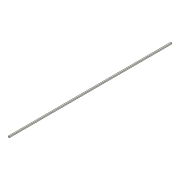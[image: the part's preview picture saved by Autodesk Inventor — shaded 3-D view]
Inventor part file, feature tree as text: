
AUTODESK INVENTOR PART (.ipt)
format: ipt  version: 2018 (Build 220112000, 112)  size: 71,680 bytes
history: native  units: in
note: dims shown in document units (in); Inventor stores cm internally (conversion verified against a paired STEP export)
features: extrude x1, sketch x1
ambient origin geometry x8: Origin, YZ Plane, XZ Plane, XY Plane, X Axis, Y Axis, Z Axis, Center Point
bodies: Solid1 (feature_tree)
feature tree (2):
  extrude  "Extrusion1"  Depth=2.0in
  sketch  "Sketch1"  dims[d0=2.0in d1=2.0in d2=284.0in d3=0.0in]
